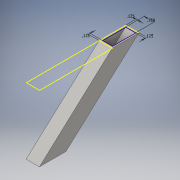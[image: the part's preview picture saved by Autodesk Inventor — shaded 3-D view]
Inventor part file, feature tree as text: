
AUTODESK INVENTOR PART (.ipt)
format: ipt  version: 2016 (Build 200138000, 138)  size: 120,832 bytes
history: native  units: in
note: dims shown in document units (in); Inventor stores cm internally (conversion verified against a paired STEP export)
features: sketch x4, extrude x1, sweep x1
ambient origin geometry x8: Origin, YZ Plane, XZ Plane, XY Plane, X Axis, Y Axis, Z Axis, Center Point
bodies: Solid1 (feature_tree)
feature tree (6):
  extrude  "Extrusion1"  Depth=1.3453in
  sketch  "Sketch4"  dims[d12=5.0in d13=1.0in d14=0.0in]
  sweep  "Sweep1"
  sketch  "Sketch3"  dims[d10=1.3453in d11=0.2905in]
  sketch  "Sketch6"  dims[d19=0.125in d20=0.125in d21=0.125in d22=0.75in d27=0.75in d28=0.125in d29=0.125in d30=0.125in d31=0.0in d32=0.0in]
  sketch  "3D Sketch1"
